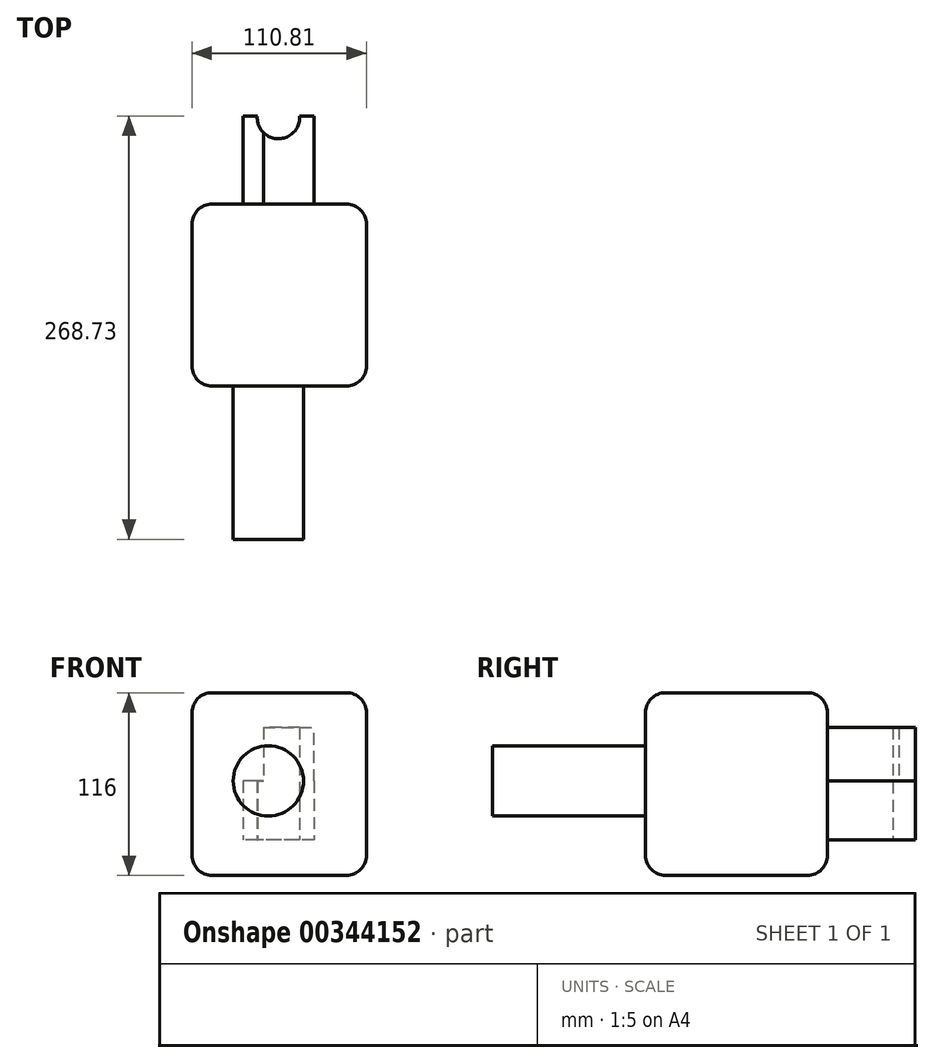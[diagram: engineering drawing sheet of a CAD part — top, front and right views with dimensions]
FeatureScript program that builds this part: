
annotation { "Feature Type Name" : "Feature", "Feature Type Description" : "" }
export const myFeature = defineFeature(function(context is Context, id is Id, definition is map)
    precondition{}
    {
        {
            var Q0;
            Q0=qCreatedBy(makeId("Front.planeOp"),FACE);
            var sketch = newSketch(context, id + "F0", { "sketchPlane" : qUnion([Q0])});
            skLineSegment(sketch, "E0.bottom", {"start": v(-57.75, 56.06) * mm, "end": v(53.06, 56.06) * mm});
            skLineSegment(sketch, "E0.top", {"start": v(-57.75, -59.94) * mm, "end": v(53.06, -59.94) * mm});
            skLineSegment(sketch, "E0.left", {"start": v(-57.75, 56.06) * mm, "end": v(-57.75, -59.94) * mm});
            skLineSegment(sketch, "E0.right", {"start": v(53.06, 56.06) * mm, "end": v(53.06, -59.94) * mm});
            skSolve(sketch);
        }
        {
            var Q0;
            Q0=makeQuery(id+"F0.imprint","IMPRINT",FACE,{"disambiguationData":[TD([[makeQuery(id+"F0.imprint","IMPRINT",EDGE,{"derivedFrom":sQuery(id+"F0.wireOp",EDGE,"E0.bottom")}),-1.0]])]});
            extrude(context, id + "F1", {"entities" : qUnion([Q0]), "depth" : 115.57 * mm});
        }
        {
            var Q0;
            Q0=makeQuery(id+"F1.opExtrude","CAP_EDGE",EDGE,{"disambiguationData":[OSD([sQuery(id+"F0.wireOp",EDGE,"E0.bottom")])],"isStart":false});
            var Q1;
            Q1=makeQuery(id+"F1.opExtrude","SWEPT_EDGE",EDGE,{"disambiguationData":[OSD([sQuery(id+"F0.wireOp",EDGE,"E0.bottom"),sQuery(id+"F0.wireOp",EDGE,"E0.right")])]});
            var Q2;
            Q2=makeQuery(id+"F1.opExtrude","CAP_EDGE",EDGE,{"disambiguationData":[OSD([sQuery(id+"F0.wireOp",EDGE,"E0.bottom")])],"isStart":true});
            var Q3;
            Q3=makeQuery(id+"F1.opExtrude","SWEPT_EDGE",EDGE,{"disambiguationData":[OSD([sQuery(id+"F0.wireOp",EDGE,"E0.bottom"),sQuery(id+"F0.wireOp",EDGE,"E0.left")])]});
            var Q4;
            Q4=makeQuery(id+"F1.opExtrude","CAP_EDGE",EDGE,{"disambiguationData":[OSD([sQuery(id+"F0.wireOp",EDGE,"E0.right")])],"isStart":false});
            var Q5;
            Q5=makeQuery(id+"F1.opExtrude","CAP_EDGE",EDGE,{"disambiguationData":[OSD([sQuery(id+"F0.wireOp",EDGE,"E0.right")])],"isStart":true});
            var Q6;
            Q6=makeQuery(id+"F1.opExtrude","CAP_EDGE",EDGE,{"disambiguationData":[OSD([sQuery(id+"F0.wireOp",EDGE,"E0.left")])],"isStart":false});
            var Q7;
            Q7=makeQuery(id+"F1.opExtrude","CAP_EDGE",EDGE,{"disambiguationData":[OSD([sQuery(id+"F0.wireOp",EDGE,"E0.left")])],"isStart":true});
            var Q8;
            Q8=makeQuery(id+"F1.opExtrude","SWEPT_EDGE",EDGE,{"disambiguationData":[OSD([sQuery(id+"F0.wireOp",EDGE,"E0.top"),sQuery(id+"F0.wireOp",EDGE,"E0.left")])]});
            var Q9;
            Q9=makeQuery(id+"F1.opExtrude","CAP_EDGE",EDGE,{"disambiguationData":[OSD([sQuery(id+"F0.wireOp",EDGE,"E0.top")])],"isStart":true});
            var Q10;
            Q10=makeQuery(id+"F1.opExtrude","CAP_EDGE",EDGE,{"disambiguationData":[OSD([sQuery(id+"F0.wireOp",EDGE,"E0.top")])],"isStart":false});
            var Q11;
            Q11=makeQuery(id+"F1.opExtrude","SWEPT_EDGE",EDGE,{"disambiguationData":[OSD([sQuery(id+"F0.wireOp",EDGE,"E0.top"),sQuery(id+"F0.wireOp",EDGE,"E0.right")])]});
            fillet(context, id + "F2", {"entities" : qUnion([Q0, Q1, Q2, Q3, Q4, Q5, Q6, Q7, Q8, Q9, Q10, Q11]), "radius" : 12.7 * mm, "tangentPropagation" : true, "allowEdgeOverflow" : false});
        }
        {
            var Q0;
            Q0=makeQuery(id+"F1.opExtrude","CAP_FACE",FACE,{"disambiguationData":[OSD([sQuery(id+"F0.wireOp",EDGE,"E0.bottom"),sQuery(id+"F0.wireOp",EDGE,"E0.top"),sQuery(id+"F0.wireOp",EDGE,"E0.left"),sQuery(id+"F0.wireOp",EDGE,"E0.right")])],"isStart":false});
            var sketch = newSketch(context, id + "F3", { "sketchPlane" : qUnion([Q0])});
            skCircle(sketch, "E1", {"center": v(-9.23, 0) * mm, "radius": 22.32 * mm});
            skSolve(sketch);
        }
        {
            var Q0;
            Q0=makeQuery(id+"F3.imprint","IMPRINT",FACE,{"disambiguationData":[TD([[makeQuery(id+"F3.imprint","IMPRINT",EDGE,{"derivedFrom":sQuery(id+"F3.wireOp",EDGE,"E1")}),1.0]])]});
            var Q1;
            Q1=sQuery(id+"F3.wireOp",EDGE,"E1");
            extrude(context, id + "F4", {"entities" : qUnion([Q0]), "surfaceEntities" : qUnion([Q1]), "depth" : 97.28 * mm});
        }
        {
            var Q0;
            Q0=makeQuery(id+"F1.opExtrude","CAP_FACE",FACE,{"disambiguationData":[OSD([sQuery(id+"F0.wireOp",EDGE,"E0.bottom"),sQuery(id+"F0.wireOp",EDGE,"E0.top"),sQuery(id+"F0.wireOp",EDGE,"E0.left"),sQuery(id+"F0.wireOp",EDGE,"E0.right")])],"isStart":true});
            var sketch = newSketch(context, id + "F5", { "sketchPlane" : qUnion([Q0])});
            skLineSegment(sketch, "E2.bottom", {"start": v(0, 0) * mm, "end": v(24.6, 0) * mm});
            skLineSegment(sketch, "E2.top", {"start": v(0, -37.34) * mm, "end": v(24.6, -37.34) * mm});
            skLineSegment(sketch, "E2.left", {"start": v(0, 0) * mm, "end": v(0, -37.34) * mm});
            skLineSegment(sketch, "E2.right", {"start": v(24.6, 0) * mm, "end": v(24.6, -37.34) * mm});
            skLineSegment(sketch, "E3.bottom", {"start": v(12.3, 0) * mm, "end": v(-19.74, 0) * mm});
            skLineSegment(sketch, "E3.top", {"start": v(12.3, 34) * mm, "end": v(-19.74, 34) * mm});
            skLineSegment(sketch, "E3.left", {"start": v(12.3, 0) * mm, "end": v(12.3, 34) * mm});
            skLineSegment(sketch, "E3.right", {"start": v(-19.74, 0) * mm, "end": v(-19.74, 34) * mm});
            skSolve(sketch);
        }
        {
            var Q0;
            Q0=makeQuery(id+"F5.imprint","IMPRINT",FACE,{"disambiguationData":[TD([[makeQuery(id+"F5.imprint","IMPRINT",EDGE,{"derivedFrom":sQuery(id+"F5.wireOp",EDGE,"E3.top")}),1.0]])]});
            var Q1;
            {var subQ1=sQuery(id+"F5.wireOp",EDGE,"E2.bottom");Q1=makeQuery(id+"F5.imprint","IMPRINT",FACE,{"disambiguationData":[TD([[makeQuery(id+"F5.imprint","IMPRINT",EDGE,{"derivedFrom":subQ1}),-1.0]])]});}
            extrude(context, id + "F6", {"entities" : qUnion([Q0, Q1]), "operationType" : NewBodyOperationType.ADD, "depth" : 109.98 * mm});
        }
        {
            var Q0;
            Q0=makeQuery(id+"F6.opExtrude","SWEPT_FACE",FACE,{"disambiguationData":[OSD([sQuery(id+"F5.wireOp",EDGE,"E2.left")])]});
            var Q1;
            Q1=makeQuery(id+"F6.opExtrude","SWEPT_FACE",FACE,{"disambiguationData":[OSD([sQuery(id+"F5.wireOp",EDGE,"E3.right")])]});
            extrude(context, id + "F7", {"entities" : qUnion([Q0, Q1]), "operationType" : NewBodyOperationType.ADD, "oppositeDirection" : true, "depth" : 25.4 * mm});
        }
        {
            var Q0;
            Q0=makeQuery(id+"F6.opExtrude","SWEPT_FACE",FACE,{"disambiguationData":[OSD([sQuery(id+"F5.wireOp",EDGE,"E2.left")])]});
            extrude(context, id + "F8", {"entities" : qUnion([Q0]), "operationType" : NewBodyOperationType.ADD, "depth" : 19.8 * mm});
        }
        {
            var Q0;
            {var subQ0=sQuery(id+"F5.wireOp",EDGE,"E2.left");var subQ1=sQuery(id+"F5.wireOp",EDGE,"E2.top");Q0=makeQuery(id+"F8.boolean.opBoolean","MERGE",FACE,{"derivedFrom":[makeQuery(id+"F7.boolean.opBoolean","MERGE",FACE,{"derivedFrom":[makeQuery(id+"F6.opExtrude","SWEPT_FACE",FACE,{"disambiguationData":[OSD([subQ1])]}),makeQuery(id+"F7.opExtrude","SWEPT_FACE",FACE,{"disambiguationData":[OSD([subQ1,subQ0])]})]}),makeQuery(id+"F8.opExtrude","SWEPT_FACE",FACE,{"disambiguationData":[OSD([subQ1,subQ0])]})]});}
            var sketch = newSketch(context, id + "F9", { "sketchPlane" : qUnion([Q0])});
            skLineSegment(sketch, "E4", {"start": v(-25.4, 0) * mm, "end": v(-25.4, -109.98) * mm});
            skCircle(sketch, "E5", {"center": v(-2.8, -55) * mm, "radius": 13.46 * mm});
            skSolve(sketch);
        }
        {
            var Q0;
            Q0=makeQuery(id+"F9.imprint","IMPRINT",FACE,{"disambiguationData":[TD([[makeQuery(id+"F9.imprint","IMPRINT",EDGE,{"derivedFrom":sQuery(id+"F9.wireOp",EDGE,"E5")}),1.0]])]});
            var Q1;
            Q1=sQuery(id+"F9.wireOp",EDGE,"E5");
            extrude(context, id + "F10", {"entities" : qUnion([Q0]), "operationType" : NewBodyOperationType.REMOVE, "surfaceEntities" : qUnion([Q1]), "oppositeDirection" : true, "depth" : 133.6 * mm});
        }
        {
            var Q0;
            {var subQ0=sQuery(id+"F5.wireOp",EDGE,"E2.left");var subQ1=makeQuery(id+"F6.opExtrude","CAP_EDGE",EDGE,{"disambiguationData":[OSD([subQ0])],"isStart":false});var subQ2=sQuery(id+"F5.wireOp",EDGE,"E3.right");Q0=makeQuery(id+"F8.boolean.opBoolean","MERGE",FACE,{"derivedFrom":[makeQuery(id+"F7.boolean.opBoolean","MERGE",FACE,{"derivedFrom":[makeQuery(id+"F6.opExtrude","CAP_FACE",FACE,{"disambiguationData":[OSD([sQuery(id+"F5.wireOp",EDGE,"E2.bottom"),sQuery(id+"F5.wireOp",EDGE,"E2.top"),subQ0,sQuery(id+"F5.wireOp",EDGE,"E2.right"),sQuery(id+"F5.wireOp",EDGE,"E3.bottom"),sQuery(id+"F5.wireOp",EDGE,"E3.top"),sQuery(id+"F5.wireOp",EDGE,"E3.left"),subQ2])],"isStart":false}),makeQuery(id+"F7.opExtrude","SWEPT_FACE",FACE,{"disambiguationData":[OSD([subQ0]),TDD([subQ1])]}),makeQuery(id+"F7.opExtrude","SWEPT_FACE",FACE,{"disambiguationData":[OSD([subQ2]),TDD([makeQuery(id+"F6.opExtrude","CAP_EDGE",EDGE,{"disambiguationData":[OSD([subQ2])],"isStart":false})])]})]}),makeQuery(id+"F8.opExtrude","SWEPT_FACE",FACE,{"disambiguationData":[OSD([subQ0]),TDD([subQ1])]})]});}
            extrude(context, id + "F11", {"entities" : qUnion([Q0]), "operationType" : NewBodyOperationType.REMOVE, "oppositeDirection" : true, "depth" : 54.1 * mm});
        }
    });
